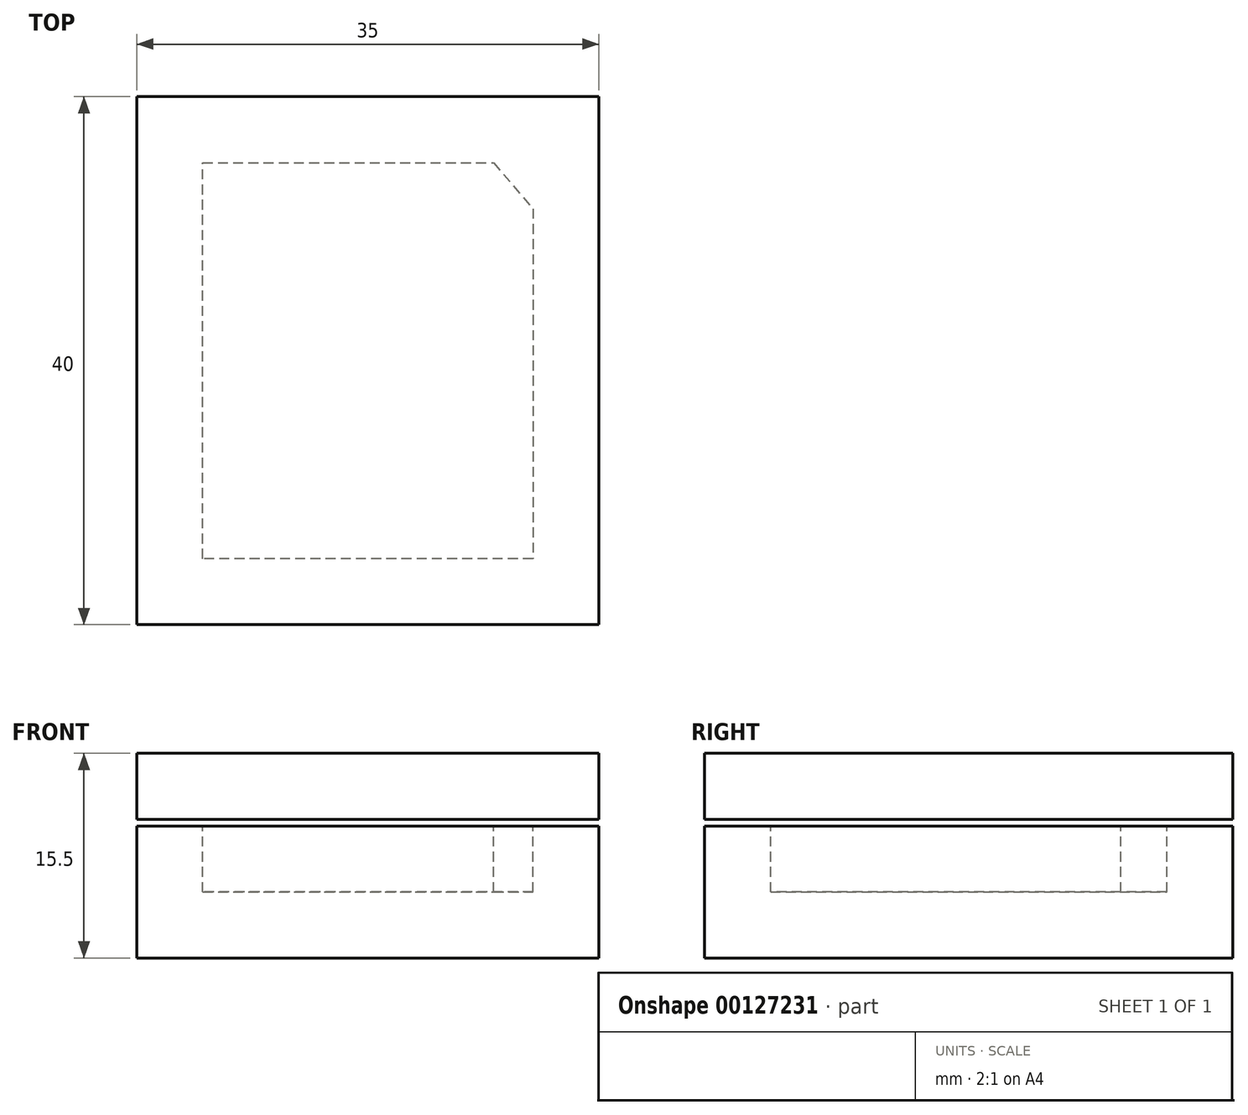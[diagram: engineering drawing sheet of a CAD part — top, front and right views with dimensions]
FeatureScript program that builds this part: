
annotation { "Feature Type Name" : "Feature", "Feature Type Description" : "" }
export const myFeature = defineFeature(function(context is Context, id is Id, definition is map)
    precondition{}
    {
        {
            var Q0;
            Q0=qCreatedBy(makeId("Top.planeOp"),FACE);
            var sketch = newSketch(context, id + "F0", { "sketchPlane" : qUnion([Q0])});
            skLineSegment(sketch, "E0.bottom", {"start": v(17.5, 20) * mm, "end": v(-17.5, 20) * mm});
            skLineSegment(sketch, "E0.top", {"start": v(17.5, -20) * mm, "end": v(-17.5, -20) * mm});
            skLineSegment(sketch, "E0.left", {"start": v(17.5, 20) * mm, "end": v(17.5, -20) * mm});
            skLineSegment(sketch, "E0.right", {"start": v(-17.5, 20) * mm, "end": v(-17.5, -20) * mm});
            skPoint(sketch, "E0.middle", {"position": v(0, 0) * mm});
            skSolve(sketch);
        }
        {
            var Q0;
            Q0=makeQuery(id+"F0.imprint","IMPRINT",FACE,{"disambiguationData":[TD([[makeQuery(id+"F0.imprint","IMPRINT",EDGE,{"derivedFrom":sQuery(id+"F0.wireOp",EDGE,"E0.bottom")}),1.0]])]});
            extrude(context, id + "F1", {"entities" : qUnion([Q0]), "depth" : 10 * mm});
        }
        {
            var Q0;
            Q0=makeQuery(id+"F1.opExtrude","CAP_FACE",FACE,{"disambiguationData":[OSD([sQuery(id+"F0.wireOp",EDGE,"E0.bottom"),sQuery(id+"F0.wireOp",EDGE,"E0.top"),sQuery(id+"F0.wireOp",EDGE,"E0.left"),sQuery(id+"F0.wireOp",EDGE,"E0.right")])],"isStart":false});
            var sketch = newSketch(context, id + "F2", { "sketchPlane" : qUnion([Q0])});
            skLineSegment(sketch, "E1.bottom", {"start": v(12.5, -15) * mm, "end": v(-12.5, -15) * mm});
            skLineSegment(sketch, "E1.right", {"start": v(-12.5, -15) * mm, "end": v(-12.5, 15) * mm});
            skPoint(sketch, "E1.middle", {"position": v(0, 0) * mm});
            skLineSegment(sketch, "E2", {"start": v(9.53, 15) * mm, "end": v(12.5, 11.51) * mm});
            skLineSegment(sketch, "E3", {"start": v(12.5, 11.51) * mm, "end": v(12.5, -15) * mm});
            skLineSegment(sketch, "E4", {"start": v(-12.5, 15) * mm, "end": v(9.53, 15) * mm});
            skSolve(sketch);
        }
        {
            var Q0;
            Q0 = qSketchRegion(id + "F2", true);
            extrude(context, id + "F3", {"entities" : qUnion([Q0]), "operationType" : NewBodyOperationType.REMOVE, "oppositeDirection" : true, "depth" : 5 * mm});
        }
        {
            var Q0;
            Q0=makeQuery(id+"F1.opExtrude","CAP_FACE",FACE,{"disambiguationData":[OSD([sQuery(id+"F0.wireOp",EDGE,"E0.bottom"),sQuery(id+"F0.wireOp",EDGE,"E0.top"),sQuery(id+"F0.wireOp",EDGE,"E0.left"),sQuery(id+"F0.wireOp",EDGE,"E0.right")])],"isStart":false});
            cPlane(context, id + "F4", {"entities" : qUnion([Q0]), "cplaneType" : CPlaneType.OFFSET, "offset" : 0.5 * mm, "width" : 150 * mm, "height" : 150 * mm});
        }
        {
            var Q0;
            Q0=qCreatedBy(id+"F4.planeOp",FACE);
            var sketch = newSketch(context, id + "F5", { "sketchPlane" : qUnion([Q0])});
            skLineSegment(sketch, "E5.bottom", {"start": v(17.5, 20) * mm, "end": v(-17.5, 20) * mm});
            skLineSegment(sketch, "E5.top", {"start": v(17.5, -20) * mm, "end": v(-17.5, -20) * mm});
            skLineSegment(sketch, "E5.left", {"start": v(17.5, 20) * mm, "end": v(17.5, -20) * mm});
            skLineSegment(sketch, "E5.right", {"start": v(-17.5, 20) * mm, "end": v(-17.5, -20) * mm});
            skPoint(sketch, "E5.middle", {"position": v(0, 0) * mm});
            skSolve(sketch);
        }
        {
            var Q0;
            Q0 = qSketchRegion(id + "F5", true);
            extrude(context, id + "F6", {"entities" : qUnion([Q0]), "depth" : 5 * mm});
        }
    });
